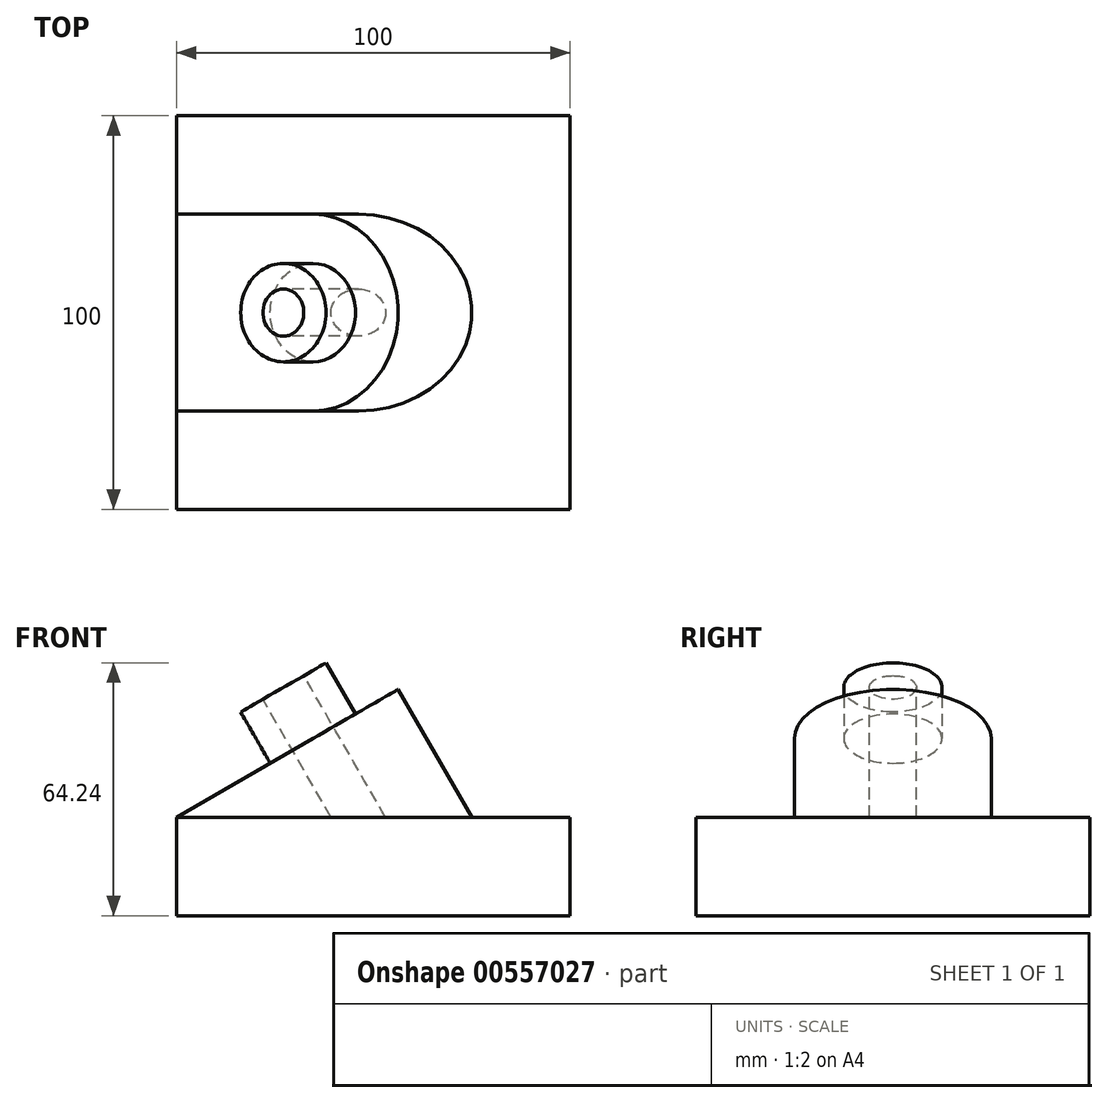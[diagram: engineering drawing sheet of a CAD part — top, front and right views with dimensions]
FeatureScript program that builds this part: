
annotation { "Feature Type Name" : "Feature", "Feature Type Description" : "" }
export const myFeature = defineFeature(function(context is Context, id is Id, definition is map)
    precondition{}
    {
        {
            var Q0;
            Q0=qCreatedBy(makeId("Front.planeOp"),FACE);
            var sketch = newSketch(context, id + "F0", { "sketchPlane" : qUnion([Q0])});
            skLineSegment(sketch, "E0.bottom", {"start": v(0, 0) * mm, "end": v(100, 0) * mm});
            skLineSegment(sketch, "E0.top", {"start": v(0, 25) * mm, "end": v(100, 25) * mm});
            skLineSegment(sketch, "E0.left", {"start": v(0, 0) * mm, "end": v(0, 25) * mm});
            skLineSegment(sketch, "E0.right", {"start": v(100, 0) * mm, "end": v(100, 25) * mm});
            skSolve(sketch);
        }
        {
            var Q0;
            Q0 = qSketchRegion(id + "F0", true);
            extrude(context, id + "F1", {"entities" : qUnion([Q0]), "oppositeDirection" : true, "depth" : 100 * mm, "offsetDistance" : 25 * mm});
        }
        {
            var Q0;
            Q0=makeQuery(id+"F1.opExtrude","SWEPT_EDGE",EDGE,{"disambiguationData":[OSD([sQuery(id+"F0.wireOp",EDGE,"E0.top"),sQuery(id+"F0.wireOp",EDGE,"E0.left")])]});
            cPlane(context, id + "F2", {"entities" : qUnion([Q0]), "cplaneType" : CPlaneType.LINE_ANGLE, "offset" : 25 * mm, "angle" : 30 * degree, "width" : 150 * mm, "height" : 150 * mm});
        }
        {
            var Q0;
            Q0=makeQuery(id+"F1.opExtrude","SWEPT_FACE",FACE,{"disambiguationData":[OSD([sQuery(id+"F0.wireOp",EDGE,"E0.top")])]});
            var sketch = newSketch(context, id + "F3", { "sketchPlane" : qUnion([Q0])});
            skLineSegment(sketch, "E1", {"start": v(0, 50) * mm, "end": v(100, 50) * mm});
            skSolve(sketch);
        }
        {
            var Q0;
            Q0=qCreatedBy(id+"F2.planeOp",FACE);
            var sketch = newSketch(context, id + "F4", { "sketchPlane" : qUnion([Q0])});
            skLineSegment(sketch, "E2", {"start": v(12.5, -75) * mm, "end": v(52.5, -75) * mm});
            skLineSegment(sketch, "E3", {"start": v(12.5, -25) * mm, "end": v(52.5, -25) * mm});
            skArc(sketch, "E4", {"start": v(52.5, -75) * mm, "mid": v(77.5, -50) * mm, "end": v(52.5, -25) * mm});
            skLineSegment(sketch, "E5", {"start": v(12.5, -75) * mm, "end": v(12.5, -25) * mm});
            skSolve(sketch);
        }
        {
            var Q0;
            Q0 = qSketchRegion(id + "F4", true);
            var Q1;
            Q1=makeQuery(id+"F1.opExtrude","SWEPT_FACE",FACE,{"disambiguationData":[OSD([sQuery(id+"F0.wireOp",EDGE,"E0.top")])]});
            extrude(context, id + "F5", {"entities" : qUnion([Q0]), "operationType" : NewBodyOperationType.ADD, "endBound" : BoundingType.UP_TO_SURFACE, "depth" : 25 * mm, "endBoundEntityFace" : qUnion([Q1]), "offsetDistance" : 25 * mm});
        }
        {
            var Q0;
            Q0=makeQuery(id+"F5.opExtrude","CAP_FACE",FACE,{"disambiguationData":[OSD([sQuery(id+"F4.wireOp",EDGE,"E2"),sQuery(id+"F4.wireOp",EDGE,"E3"),sQuery(id+"F4.wireOp",EDGE,"E4"),sQuery(id+"F4.wireOp",EDGE,"E5")])],"isStart":true});
            var sketch = newSketch(context, id + "F6", { "sketchPlane" : qUnion([Q0])});
            skCircle(sketch, "E6", {"center": v(52.5, 50) * mm, "radius": 12.5 * mm});
            skSolve(sketch);
        }
        {
            var Q0;
            Q0 = qSketchRegion(id + "F6", true);
            extrude(context, id + "F7", {"entities" : qUnion([Q0]), "operationType" : NewBodyOperationType.ADD, "depth" : 15 * mm, "offsetDistance" : 25 * mm});
        }
        {
            var Q0;
            Q0=makeQuery(id+"F7.opExtrude","CAP_FACE",FACE,{"disambiguationData":[OSD([sQuery(id+"F6.wireOp",EDGE,"E6")])],"isStart":false});
            var sketch = newSketch(context, id + "F8", { "sketchPlane" : qUnion([Q0])});
            skCircle(sketch, "E7", {"center": v(52.5, 50) * mm, "radius": 6 * mm});
            skSolve(sketch);
        }
        {
            var Q0;
            Q0 = qSketchRegion(id + "F8", true);
            var Q1;
            Q1=makeQuery(id+"F1.opExtrude","SWEPT_FACE",FACE,{"disambiguationData":[OSD([sQuery(id+"F0.wireOp",EDGE,"E0.top")])]});
            extrude(context, id + "F9", {"entities" : qUnion([Q0]), "operationType" : NewBodyOperationType.REMOVE, "endBound" : BoundingType.UP_TO_SURFACE, "oppositeDirection" : true, "depth" : 25 * mm, "endBoundEntityFace" : qUnion([Q1]), "offsetDistance" : 25 * mm});
        }
    });
